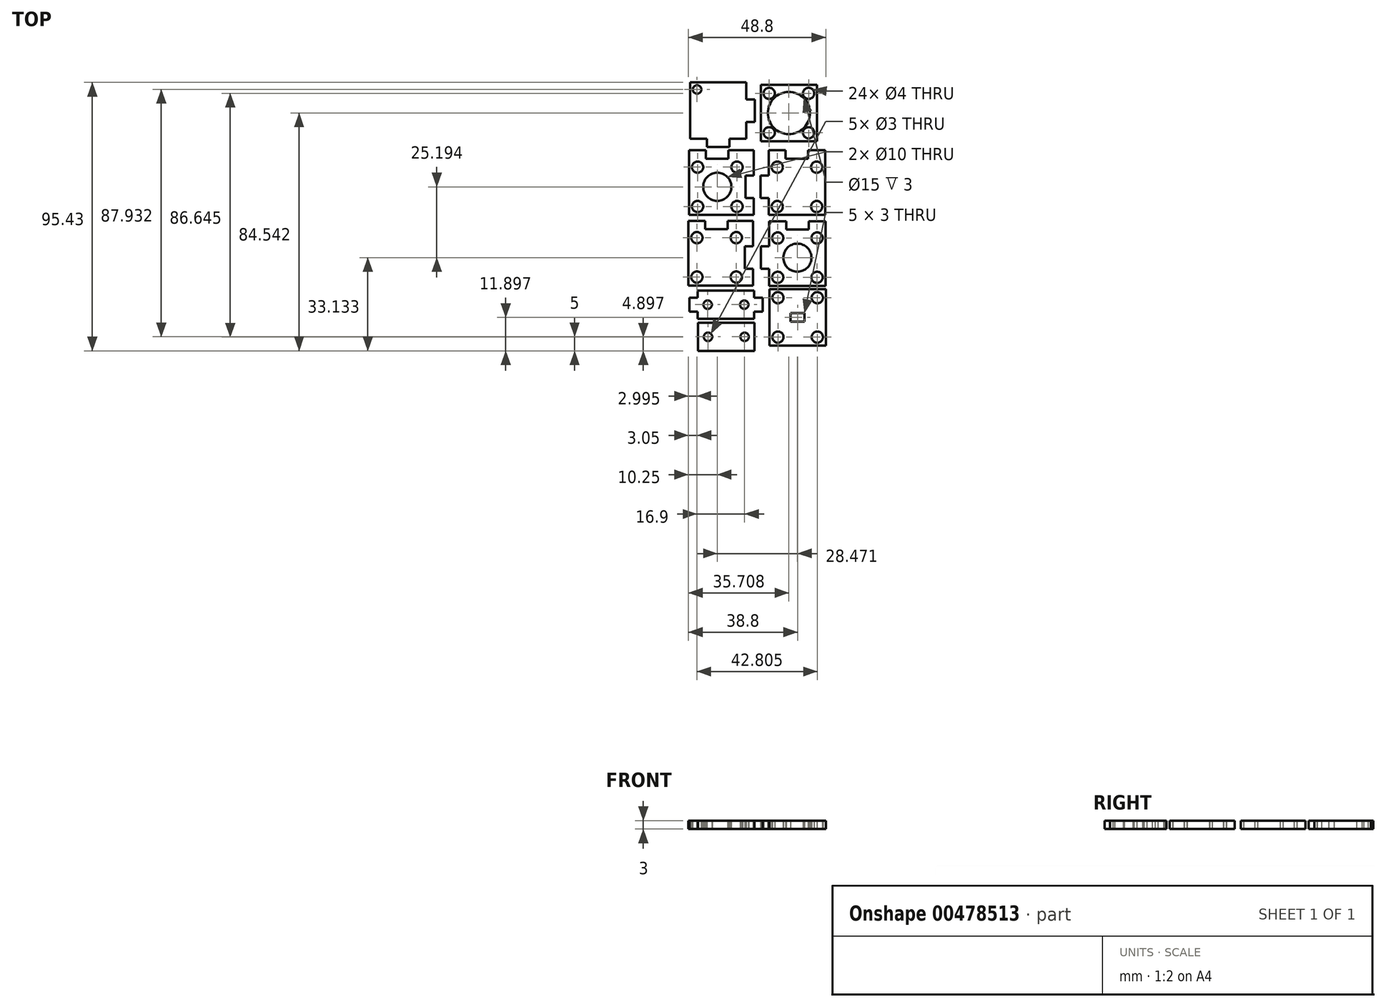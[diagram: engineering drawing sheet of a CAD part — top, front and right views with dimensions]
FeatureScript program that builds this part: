
annotation { "Feature Type Name" : "Feature", "Feature Type Description" : "" }
export const myFeature = defineFeature(function(context is Context, id is Id, definition is map)
    precondition{}
    {
        {
            var Q0;
            Q0=qCreatedBy(makeId("Top.planeOp"),FACE);
            var sketch = newSketch(context, id + "F0", { "sketchPlane" : qUnion([Q0])});
            skLineSegment(sketch, "E0.bottom", {"start": v(71.06, 44.84) * mm, "end": v(51.06, 44.84) * mm});
            skLineSegment(sketch, "E0.top", {"start": v(71.06, 64.84) * mm, "end": v(51.06, 64.84) * mm});
            skLineSegment(sketch, "E0.left", {"start": v(71.06, 44.84) * mm, "end": v(71.06, 64.84) * mm});
            skLineSegment(sketch, "E0.right", {"start": v(51.06, 44.84) * mm, "end": v(51.06, 64.84) * mm});
            skCircle(sketch, "E1", {"center": v(61.06, 54.84) * mm, "radius": 7.5 * mm});
            skCircle(sketch, "E2", {"center": v(68.06, 61.84) * mm, "radius": 2 * mm});
            skCircle(sketch, "E3.MirrorC", {"center": v(54.06, 61.84) * mm, "radius": 2 * mm});
            skCircle(sketch, "E4.MirrorC", {"center": v(68.06, 47.84) * mm, "radius": 2 * mm});
            skCircle(sketch, "E5.MirrorC", {"center": v(54.06, 47.84) * mm, "radius": 2 * mm});
            skSolve(sketch);
        }
        {
            var Q0;
            Q0=makeQuery(id+"F0.imprint","IMPRINT",FACE,{"disambiguationData":[TD([[makeQuery(id+"F0.imprint","IMPRINT",EDGE,{"derivedFrom":sQuery(id+"F0.wireOp",EDGE,"E0.bottom")}),-1.0]])]});
            extrude(context, id + "F1", {"entities" : qUnion([Q0]), "depth" : 3 * mm});
        }
        {
            var Q0;
            Q0=qCreatedBy(makeId("Top.planeOp"),FACE);
            var sketch = newSketch(context, id + "F2", { "sketchPlane" : qUnion([Q0])});
            skLineSegment(sketch, "E6.bottom", {"start": v(45.6, 18.63) * mm, "end": v(25.6, 18.63) * mm});
            skLineSegment(sketch, "E6.right", {"start": v(25.6, 18.63) * mm, "end": v(25.6, 38.63) * mm});
            skCircle(sketch, "E7", {"center": v(42.6, 35.63) * mm, "radius": 2 * mm});
            skCircle(sketch, "E8.MirrorC", {"center": v(28.6, 35.63) * mm, "radius": 2 * mm});
            skCircle(sketch, "E9.MirrorC", {"center": v(42.6, 21.63) * mm, "radius": 2 * mm});
            skCircle(sketch, "E10.MirrorC", {"center": v(28.6, 21.63) * mm, "radius": 2 * mm});
            skCircle(sketch, "E11", {"center": v(35.6, 28.63) * mm, "radius": 5 * mm});
            skLineSegment(sketch, "E12.top", {"start": v(25.6, 41.63) * mm, "end": v(31.6, 41.63) * mm});
            skLineSegment(sketch, "E12.left", {"start": v(25.6, 38.63) * mm, "end": v(25.6, 41.63) * mm});
            skLineSegment(sketch, "E12.right", {"start": v(31.6, 38.63) * mm, "end": v(31.6, 41.63) * mm});
            skLineSegment(sketch, "E13.bottom", {"start": v(45.6, 18.63) * mm, "end": v(48.6, 18.63) * mm});
            skLineSegment(sketch, "E13.top", {"start": v(45.6, 24.63) * mm, "end": v(48.6, 24.63) * mm});
            skLineSegment(sketch, "E13.right", {"start": v(48.6, 18.63) * mm, "end": v(48.6, 24.63) * mm});
            skLineSegment(sketch, "E14.top", {"start": v(45.6, 32.63) * mm, "end": v(48.6, 32.63) * mm});
            skLineSegment(sketch, "E14.right", {"start": v(48.6, 38.63) * mm, "end": v(48.6, 32.63) * mm});
            skLineSegment(sketch, "E15.top", {"start": v(48.6, 41.63) * mm, "end": v(39.6, 41.63) * mm});
            skLineSegment(sketch, "E15.left", {"start": v(48.6, 38.63) * mm, "end": v(48.6, 41.63) * mm});
            skLineSegment(sketch, "E15.right", {"start": v(39.6, 38.63) * mm, "end": v(39.6, 41.63) * mm});
            skLineSegment(sketch, "E16", {"start": v(31.6, 38.63) * mm, "end": v(39.6, 38.63) * mm});
            skLineSegment(sketch, "E17", {"start": v(45.6, 32.63) * mm, "end": v(45.6, 24.63) * mm});
            skSolve(sketch);
        }
        {
            var Q0;
            Q0 = qSketchRegion(id + "F2", true);
            extrude(context, id + "F3", {"entities" : qUnion([Q0]), "operationType" : NewBodyOperationType.ADD, "depth" : 3 * mm});
        }
        {
            var Q0;
            Q0=qCreatedBy(makeId("Top.planeOp"),FACE);
            var sketch = newSketch(context, id + "F4", { "sketchPlane" : qUnion([Q0])});
            skLineSegment(sketch, "E18.bottom", {"start": v(25.9, 65.73) * mm, "end": v(25.9, 45.73) * mm});
            skLineSegment(sketch, "E18.left", {"start": v(25.9, 65.73) * mm, "end": v(45.9, 65.73) * mm});
            skPoint(sketch, "E18.middle", {"position": v(35.9, 55.73) * mm});
            skLineSegment(sketch, "E19.bottom", {"start": v(39.9, 45.73) * mm, "end": v(39.9, 42.73) * mm});
            skLineSegment(sketch, "E19.top", {"start": v(31.9, 45.73) * mm, "end": v(31.9, 42.73) * mm});
            skLineSegment(sketch, "E19.right", {"start": v(39.9, 42.73) * mm, "end": v(31.9, 42.73) * mm});
            skLineSegment(sketch, "E20.bottom", {"start": v(45.9, 59.73) * mm, "end": v(48.9, 59.73) * mm});
            skLineSegment(sketch, "E20.top", {"start": v(45.9, 51.73) * mm, "end": v(48.9, 51.73) * mm});
            skLineSegment(sketch, "E20.right", {"start": v(48.9, 59.73) * mm, "end": v(48.9, 51.73) * mm});
            skLineSegment(sketch, "E21", {"start": v(45.9, 65.73) * mm, "end": v(45.9, 59.73) * mm});
            skLineSegment(sketch, "E22", {"start": v(25.9, 45.73) * mm, "end": v(31.9, 45.73) * mm});
            skLineSegment(sketch, "E23", {"start": v(39.9, 45.73) * mm, "end": v(45.9, 45.73) * mm});
            skLineSegment(sketch, "E24", {"start": v(45.9, 45.73) * mm, "end": v(45.9, 51.73) * mm});
            skCircle(sketch, "E25", {"center": v(28.4, 63.23) * mm, "radius": 1.5 * mm});
            skSolve(sketch);
        }
        {
            var Q0;
            Q0 = qSketchRegion(id + "F4", true);
            extrude(context, id + "F5", {"entities" : qUnion([Q0]), "operationType" : NewBodyOperationType.ADD, "depth" : 3 * mm});
        }
        {
            var Q0;
            Q0=qCreatedBy(makeId("Top.planeOp"),FACE);
            var sketch = newSketch(context, id + "F6", { "sketchPlane" : qUnion([Q0])});
            skLineSegment(sketch, "E26.top", {"start": v(73.92, 18.6) * mm, "end": v(53.92, 18.6) * mm});
            skLineSegment(sketch, "E26.left", {"start": v(73.92, 38.6) * mm, "end": v(73.92, 18.6) * mm});
            skPoint(sketch, "E26.middle", {"position": v(63.92, 28.6) * mm});
            skLineSegment(sketch, "E27.bottom", {"start": v(53.92, 24.6) * mm, "end": v(50.92, 24.6) * mm});
            skLineSegment(sketch, "E27.top", {"start": v(53.92, 32.6) * mm, "end": v(50.92, 32.6) * mm});
            skLineSegment(sketch, "E27.right", {"start": v(50.92, 24.6) * mm, "end": v(50.92, 32.6) * mm});
            skLineSegment(sketch, "E28.left", {"start": v(53.92, 38.6) * mm, "end": v(53.92, 41.6) * mm});
            skLineSegment(sketch, "E28.right", {"start": v(73.92, 38.6) * mm, "end": v(73.92, 41.6) * mm});
            skLineSegment(sketch, "E29.bottom", {"start": v(53.92, 41.6) * mm, "end": v(59.92, 41.6) * mm});
            skLineSegment(sketch, "E29.left", {"start": v(53.92, 41.6) * mm, "end": v(53.92, 38.6) * mm});
            skLineSegment(sketch, "E29.right", {"start": v(59.92, 41.6) * mm, "end": v(59.92, 38.6) * mm});
            skLineSegment(sketch, "E30.bottom", {"start": v(73.92, 41.6) * mm, "end": v(67.92, 41.6) * mm});
            skLineSegment(sketch, "E30.left", {"start": v(73.92, 41.6) * mm, "end": v(73.92, 38.6) * mm});
            skLineSegment(sketch, "E30.right", {"start": v(67.92, 41.6) * mm, "end": v(67.92, 38.6) * mm});
            skLineSegment(sketch, "E31", {"start": v(67.92, 38.6) * mm, "end": v(59.92, 38.6) * mm});
            skLineSegment(sketch, "E32", {"start": v(53.92, 38.6) * mm, "end": v(53.92, 32.6) * mm});
            skLineSegment(sketch, "E33", {"start": v(53.92, 24.6) * mm, "end": v(53.92, 18.6) * mm});
            skCircle(sketch, "E34", {"center": v(56.92, 21.6) * mm, "radius": 2 * mm});
            skLineSegment(sketch, "E35", {"start": v(63.92, 18.6) * mm, "end": v(63.92, 38.6) * mm, "construction": true});
            skLineSegment(sketch, "E36", {"start": v(73.92, 28.6) * mm, "end": v(50.92, 28.6) * mm, "construction": true});
            skCircle(sketch, "E37.MirrorC", {"center": v(70.92, 21.6) * mm, "radius": 2 * mm});
            skCircle(sketch, "E38.MirrorC", {"center": v(70.92, 35.6) * mm, "radius": 2 * mm});
            skCircle(sketch, "E39.MirrorC", {"center": v(56.92, 35.6) * mm, "radius": 2 * mm});
            skSolve(sketch);
        }
        {
            var Q0;
            Q0 = qSketchRegion(id + "F6", true);
            extrude(context, id + "F7", {"entities" : qUnion([Q0]), "operationType" : NewBodyOperationType.ADD, "depth" : 3 * mm});
        }
        {
            var Q0;
            Q0=qCreatedBy(makeId("Top.planeOp"),FACE);
            var sketch = newSketch(context, id + "F8", { "sketchPlane" : qUnion([Q0])});
            skLineSegment(sketch, "E40.top", {"start": v(74.07, -6.57) * mm, "end": v(54.07, -6.57) * mm});
            skLineSegment(sketch, "E40.left", {"start": v(74.07, 13.43) * mm, "end": v(74.07, -6.57) * mm});
            skPoint(sketch, "E40.middle", {"position": v(64.07, 3.43) * mm});
            skLineSegment(sketch, "E41.bottom", {"start": v(54.07, -0.57) * mm, "end": v(51.07, -0.57) * mm});
            skLineSegment(sketch, "E41.top", {"start": v(54.07, 7.43) * mm, "end": v(51.07, 7.43) * mm});
            skLineSegment(sketch, "E41.right", {"start": v(51.07, -0.57) * mm, "end": v(51.07, 7.43) * mm});
            skLineSegment(sketch, "E42.left", {"start": v(54.07, 13.43) * mm, "end": v(54.07, 16.43) * mm});
            skLineSegment(sketch, "E42.right", {"start": v(74.07, 13.43) * mm, "end": v(74.07, 16.43) * mm});
            skLineSegment(sketch, "E43.bottom", {"start": v(54.07, 16.43) * mm, "end": v(60.07, 16.43) * mm});
            skLineSegment(sketch, "E43.left", {"start": v(54.07, 16.43) * mm, "end": v(54.07, 13.43) * mm});
            skLineSegment(sketch, "E43.right", {"start": v(60.07, 16.43) * mm, "end": v(60.07, 13.43) * mm});
            skLineSegment(sketch, "E44.bottom", {"start": v(74.07, 16.43) * mm, "end": v(68.07, 16.43) * mm});
            skLineSegment(sketch, "E44.left", {"start": v(74.07, 16.43) * mm, "end": v(74.07, 13.43) * mm});
            skLineSegment(sketch, "E44.right", {"start": v(68.07, 16.43) * mm, "end": v(68.07, 13.43) * mm});
            skLineSegment(sketch, "E45", {"start": v(68.07, 13.43) * mm, "end": v(60.07, 13.43) * mm});
            skLineSegment(sketch, "E46", {"start": v(54.07, 13.43) * mm, "end": v(54.07, 7.43) * mm});
            skLineSegment(sketch, "E47", {"start": v(54.07, -0.57) * mm, "end": v(54.07, -6.57) * mm});
            skCircle(sketch, "E48", {"center": v(57.07, -3.57) * mm, "radius": 2 * mm});
            skLineSegment(sketch, "E49", {"start": v(64.07, -6.57) * mm, "end": v(64.07, 13.43) * mm, "construction": true});
            skLineSegment(sketch, "E50", {"start": v(74.07, 3.43) * mm, "end": v(51.07, 3.43) * mm, "construction": true});
            skCircle(sketch, "E51.MirrorC", {"center": v(71.07, -3.57) * mm, "radius": 2 * mm});
            skCircle(sketch, "E52.MirrorC", {"center": v(71.07, 10.43) * mm, "radius": 2 * mm});
            skCircle(sketch, "E53.MirrorC", {"center": v(57.07, 10.43) * mm, "radius": 2 * mm});
            skCircle(sketch, "E54", {"center": v(64.07, 3.43) * mm, "radius": 5 * mm});
            skSolve(sketch);
        }
        {
            var Q0;
            Q0 = qSketchRegion(id + "F8", true);
            extrude(context, id + "F9", {"entities" : qUnion([Q0]), "depth" : 3 * mm});
        }
        {
            var Q0;
            Q0=qCreatedBy(makeId("Top.planeOp"),FACE);
            var sketch = newSketch(context, id + "F10", { "sketchPlane" : qUnion([Q0])});
            skLineSegment(sketch, "E55.bottom", {"start": v(45.35, -6.45) * mm, "end": v(25.35, -6.45) * mm});
            skLineSegment(sketch, "E55.right", {"start": v(25.35, -6.45) * mm, "end": v(25.35, 13.55) * mm});
            skCircle(sketch, "E56", {"center": v(42.35, 10.55) * mm, "radius": 2 * mm});
            skCircle(sketch, "E57.MirrorC", {"center": v(28.35, 10.55) * mm, "radius": 2 * mm});
            skCircle(sketch, "E58.MirrorC", {"center": v(42.35, -3.45) * mm, "radius": 2 * mm});
            skCircle(sketch, "E59.MirrorC", {"center": v(28.35, -3.45) * mm, "radius": 2 * mm});
            skLineSegment(sketch, "E60.top", {"start": v(25.35, 16.55) * mm, "end": v(31.35, 16.55) * mm});
            skLineSegment(sketch, "E60.left", {"start": v(25.35, 13.55) * mm, "end": v(25.35, 16.55) * mm});
            skLineSegment(sketch, "E60.right", {"start": v(31.35, 13.55) * mm, "end": v(31.35, 16.55) * mm});
            skLineSegment(sketch, "E61.bottom", {"start": v(45.35, -6.45) * mm, "end": v(48.35, -6.45) * mm});
            skLineSegment(sketch, "E61.top", {"start": v(45.35, -0.45) * mm, "end": v(48.35, -0.45) * mm});
            skLineSegment(sketch, "E61.right", {"start": v(48.35, -6.45) * mm, "end": v(48.35, -0.45) * mm});
            skLineSegment(sketch, "E62.top", {"start": v(45.35, 7.55) * mm, "end": v(48.35, 7.55) * mm});
            skLineSegment(sketch, "E62.right", {"start": v(48.35, 13.55) * mm, "end": v(48.35, 7.55) * mm});
            skLineSegment(sketch, "E63.top", {"start": v(48.35, 16.55) * mm, "end": v(39.35, 16.55) * mm});
            skLineSegment(sketch, "E63.left", {"start": v(48.35, 13.55) * mm, "end": v(48.35, 16.55) * mm});
            skLineSegment(sketch, "E63.right", {"start": v(39.35, 13.55) * mm, "end": v(39.35, 16.55) * mm});
            skLineSegment(sketch, "E64", {"start": v(31.35, 13.55) * mm, "end": v(39.35, 13.55) * mm});
            skLineSegment(sketch, "E65", {"start": v(45.35, 7.55) * mm, "end": v(45.35, -0.45) * mm});
            skSolve(sketch);
        }
        {
            var Q0;
            Q0 = qSketchRegion(id + "F10", true);
            extrude(context, id + "F11", {"entities" : qUnion([Q0]), "depth" : 3 * mm});
        }
        {
            var Q0;
            Q0=qCreatedBy(makeId("Top.planeOp"),FACE);
            var sketch = newSketch(context, id + "F12", { "sketchPlane" : qUnion([Q0])});
            skLineSegment(sketch, "E66.bottom", {"start": v(74.15, -7.8) * mm, "end": v(54.15, -7.8) * mm});
            skLineSegment(sketch, "E66.top", {"start": v(74.15, -27.8) * mm, "end": v(54.15, -27.8) * mm});
            skLineSegment(sketch, "E66.left", {"start": v(74.15, -7.8) * mm, "end": v(74.15, -27.8) * mm});
            skLineSegment(sketch, "E66.right", {"start": v(54.15, -7.8) * mm, "end": v(54.15, -27.8) * mm});
            skPoint(sketch, "E66.middle", {"position": v(64.15, -17.8) * mm});
            skLineSegment(sketch, "E67", {"start": v(64.15, -7.8) * mm, "end": v(64.15, -27.8) * mm, "construction": true});
            skLineSegment(sketch, "E68", {"start": v(74.15, -17.8) * mm, "end": v(54.15, -17.8) * mm, "construction": true});
            skCircle(sketch, "E69", {"center": v(57.15, -10.8) * mm, "radius": 2 * mm});
            skCircle(sketch, "E70.MirrorC", {"center": v(71.15, -10.8) * mm, "radius": 2 * mm});
            skCircle(sketch, "E71.MirrorC", {"center": v(71.15, -24.8) * mm, "radius": 2 * mm});
            skCircle(sketch, "E72.MirrorC", {"center": v(57.15, -24.8) * mm, "radius": 2 * mm});
            skLineSegment(sketch, "E73.bottom", {"start": v(66.65, -16.3) * mm, "end": v(61.65, -16.3) * mm});
            skLineSegment(sketch, "E73.top", {"start": v(66.65, -19.3) * mm, "end": v(61.65, -19.3) * mm});
            skLineSegment(sketch, "E73.left", {"start": v(66.65, -16.3) * mm, "end": v(66.65, -19.3) * mm});
            skLineSegment(sketch, "E73.right", {"start": v(61.65, -16.3) * mm, "end": v(61.65, -19.3) * mm});
            skSolve(sketch);
        }
        {
            var Q0;
            Q0 = qSketchRegion(id + "F12", true);
            extrude(context, id + "F13", {"entities" : qUnion([Q0]), "depth" : 3 * mm});
        }
        {
            var Q0;
            Q0=qCreatedBy(makeId("Top.planeOp"),FACE);
            var sketch = newSketch(context, id + "F14", { "sketchPlane" : qUnion([Q0])});
            skLineSegment(sketch, "E74.left", {"start": v(28.68, -8.26) * mm, "end": v(48.68, -8.26) * mm});
            skLineSegment(sketch, "E74.right", {"start": v(28.68, -18.26) * mm, "end": v(48.68, -18.26) * mm});
            skPoint(sketch, "E74.middle", {"position": v(38.68, -13.26) * mm});
            skLineSegment(sketch, "E75.top", {"start": v(25.68, -15.76) * mm, "end": v(25.68, -10.76) * mm});
            skLineSegment(sketch, "E75.left", {"start": v(28.68, -15.76) * mm, "end": v(25.68, -15.76) * mm});
            skLineSegment(sketch, "E75.right", {"start": v(28.68, -10.76) * mm, "end": v(25.68, -10.76) * mm});
            skLineSegment(sketch, "E76.top", {"start": v(51.68, -15.76) * mm, "end": v(51.68, -10.76) * mm});
            skLineSegment(sketch, "E76.left", {"start": v(48.68, -15.76) * mm, "end": v(51.68, -15.76) * mm});
            skLineSegment(sketch, "E76.right", {"start": v(48.68, -10.76) * mm, "end": v(51.68, -10.76) * mm});
            skCircle(sketch, "E77", {"center": v(32.18, -13.26) * mm, "radius": 1.5 * mm});
            skLineSegment(sketch, "E78", {"start": v(38.68, -18.26) * mm, "end": v(38.68, -8.26) * mm, "construction": true});
            skCircle(sketch, "E79.MirrorC", {"center": v(45.18, -13.26) * mm, "radius": 1.5 * mm});
            skLineSegment(sketch, "E80", {"start": v(28.68, -18.26) * mm, "end": v(28.68, -15.76) * mm});
            skLineSegment(sketch, "E81", {"start": v(28.68, -10.76) * mm, "end": v(28.68, -8.26) * mm});
            skLineSegment(sketch, "E82", {"start": v(48.68, -8.26) * mm, "end": v(48.68, -10.76) * mm});
            skLineSegment(sketch, "E83", {"start": v(48.68, -15.76) * mm, "end": v(48.68, -18.26) * mm});
            skSolve(sketch);
        }
        {
            var Q0;
            Q0 = qSketchRegion(id + "F14", true);
            extrude(context, id + "F15", {"entities" : qUnion([Q0]), "depth" : 3 * mm});
        }
        {
            var Q0;
            Q0=qCreatedBy(makeId("Top.planeOp"),FACE);
            var sketch = newSketch(context, id + "F16", { "sketchPlane" : qUnion([Q0])});
            skLineSegment(sketch, "E84.left", {"start": v(28.8, -19.7) * mm, "end": v(48.8, -19.7) * mm});
            skLineSegment(sketch, "E84.right", {"start": v(28.8, -29.7) * mm, "end": v(48.8, -29.7) * mm});
            skPoint(sketch, "E84.middle", {"position": v(38.8, -24.7) * mm});
            skCircle(sketch, "E85", {"center": v(32.3, -24.7) * mm, "radius": 1.5 * mm});
            skLineSegment(sketch, "E86", {"start": v(38.8, -29.7) * mm, "end": v(38.8, -19.7) * mm, "construction": true});
            skCircle(sketch, "E87.MirrorC", {"center": v(45.3, -24.7) * mm, "radius": 1.5 * mm});
            skLineSegment(sketch, "E88", {"start": v(28.8, -29.7) * mm, "end": v(28.8, -27.2) * mm});
            skLineSegment(sketch, "E89", {"start": v(28.8, -22.2) * mm, "end": v(28.8, -19.7) * mm});
            skLineSegment(sketch, "E90", {"start": v(48.8, -19.7) * mm, "end": v(48.8, -22.2) * mm});
            skLineSegment(sketch, "E91", {"start": v(48.8, -27.2) * mm, "end": v(48.8, -29.7) * mm});
            skLineSegment(sketch, "E92", {"start": v(28.8, -27.2) * mm, "end": v(28.8, -22.2) * mm});
            skLineSegment(sketch, "E93", {"start": v(48.8, -22.2) * mm, "end": v(48.8, -27.2) * mm});
            skSolve(sketch);
        }
        {
            var Q0;
            Q0 = qSketchRegion(id + "F16", true);
            extrude(context, id + "F17", {"entities" : qUnion([Q0]), "depth" : 3 * mm});
        }
    });
